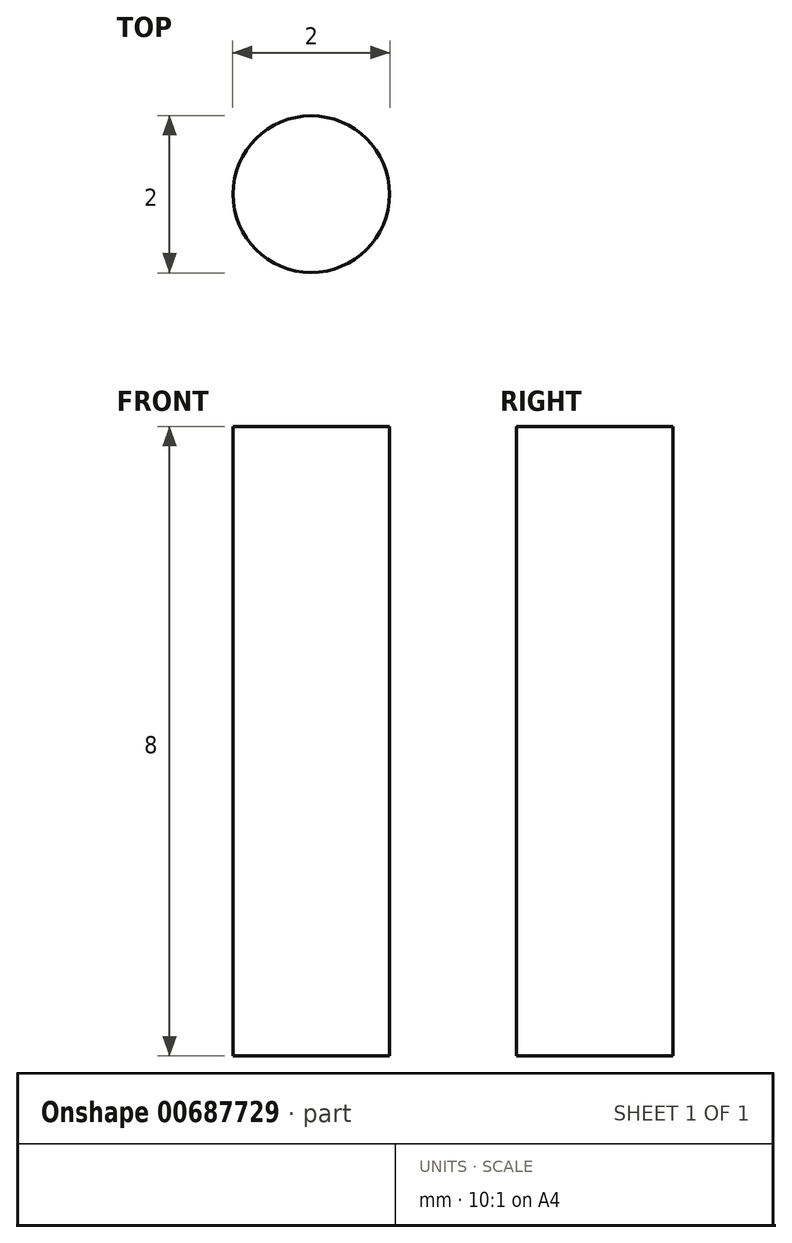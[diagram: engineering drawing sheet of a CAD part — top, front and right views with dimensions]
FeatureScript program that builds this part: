
annotation { "Feature Type Name" : "Feature", "Feature Type Description" : "" }
export const myFeature = defineFeature(function(context is Context, id is Id, definition is map)
    precondition{}
    {
        {
            var Q0;
            Q0=qCreatedBy(makeId("Top.planeOp"),FACE);
            var sketch = newSketch(context, id + "F0", { "sketchPlane" : qUnion([Q0])});
            skLineSegment(sketch, "E0.bottom", {"start": v(0, 0) * mm, "end": v(3.2, 0) * mm});
            skLineSegment(sketch, "E0.top", {"start": v(0, 3.2) * mm, "end": v(3.2, 3.2) * mm});
            skLineSegment(sketch, "E0.left", {"start": v(0, 0) * mm, "end": v(0, 3.2) * mm});
            skLineSegment(sketch, "E0.right", {"start": v(3.2, 0) * mm, "end": v(3.2, 3.2) * mm});
            skSolve(sketch);
        }
        {
            var Q0;
            Q0=makeQuery(id+"F0.imprint","IMPRINT",FACE,{"disambiguationData":[TD([[makeQuery(id+"F0.imprint","IMPRINT",EDGE,{"derivedFrom":sQuery(id+"F0.wireOp",EDGE,"E0.bottom")}),1.0]])]});
            extrude(context, id + "F1", {"entities" : qUnion([Q0]), "depth" : 8 * mm, "offsetDistance" : 25 * mm});
        }
        {
            var Q0;
            Q0=makeQuery(id+"F1.opExtrude","CAP_FACE",FACE,{"disambiguationData":[OSD([sQuery(id+"F0.wireOp",EDGE,"E0.bottom"),sQuery(id+"F0.wireOp",EDGE,"E0.top"),sQuery(id+"F0.wireOp",EDGE,"E0.left"),sQuery(id+"F0.wireOp",EDGE,"E0.right")])],"isStart":false});
            var sketch = newSketch(context, id + "F2", { "sketchPlane" : qUnion([Q0])});
            skLineSegment(sketch, "E1", {"start": v(0, 3.2) * mm, "end": v(3.2, 0) * mm});
            skCircle(sketch, "E2", {"center": v(1.6, 1.6) * mm, "radius": 1 * mm});
            skSolve(sketch);
        }
        {
            var Q0;
            {var subQ0=sQuery(id+"F2.wireOp",EDGE,"E2");var subQ1=sQuery(id+"F2.wireOp",EDGE,"E1");var subQ2=makeQuery(id+"F2.imprint","INTERSECT",VERTEX,{"disambiguationData":[OD(0.0)],"derivedFrom":[subQ1,subQ0]});Q0=makeQuery(id+"F2.imprint","IMPRINT",FACE,{"disambiguationData":[TD([[makeQuery(id+"F2.imprint","IMPRINT",EDGE,{"disambiguationData":[TD([[subQ2,-1.0]])],"derivedFrom":subQ1}),-1.0]])]});}
            var Q1;
            {var subQ0=sQuery(id+"F2.wireOp",EDGE,"E2");var subQ1=sQuery(id+"F2.wireOp",EDGE,"E1");var subQ2=makeQuery(id+"F2.imprint","INTERSECT",VERTEX,{"disambiguationData":[OD(0.0)],"derivedFrom":[subQ1,subQ0]});Q1=makeQuery(id+"F2.imprint","IMPRINT",FACE,{"disambiguationData":[TD([[makeQuery(id+"F2.imprint","IMPRINT",EDGE,{"disambiguationData":[TD([[subQ2,-1.0]])],"derivedFrom":subQ1}),1.0]])]});}
            extrude(context, id + "F3", {"entities" : qUnion([Q0, Q1]), "operationType" : NewBodyOperationType.REMOVE, "oppositeDirection" : true, "depth" : 25 * mm, "offsetDistance" : 25 * mm});
        }
    });
